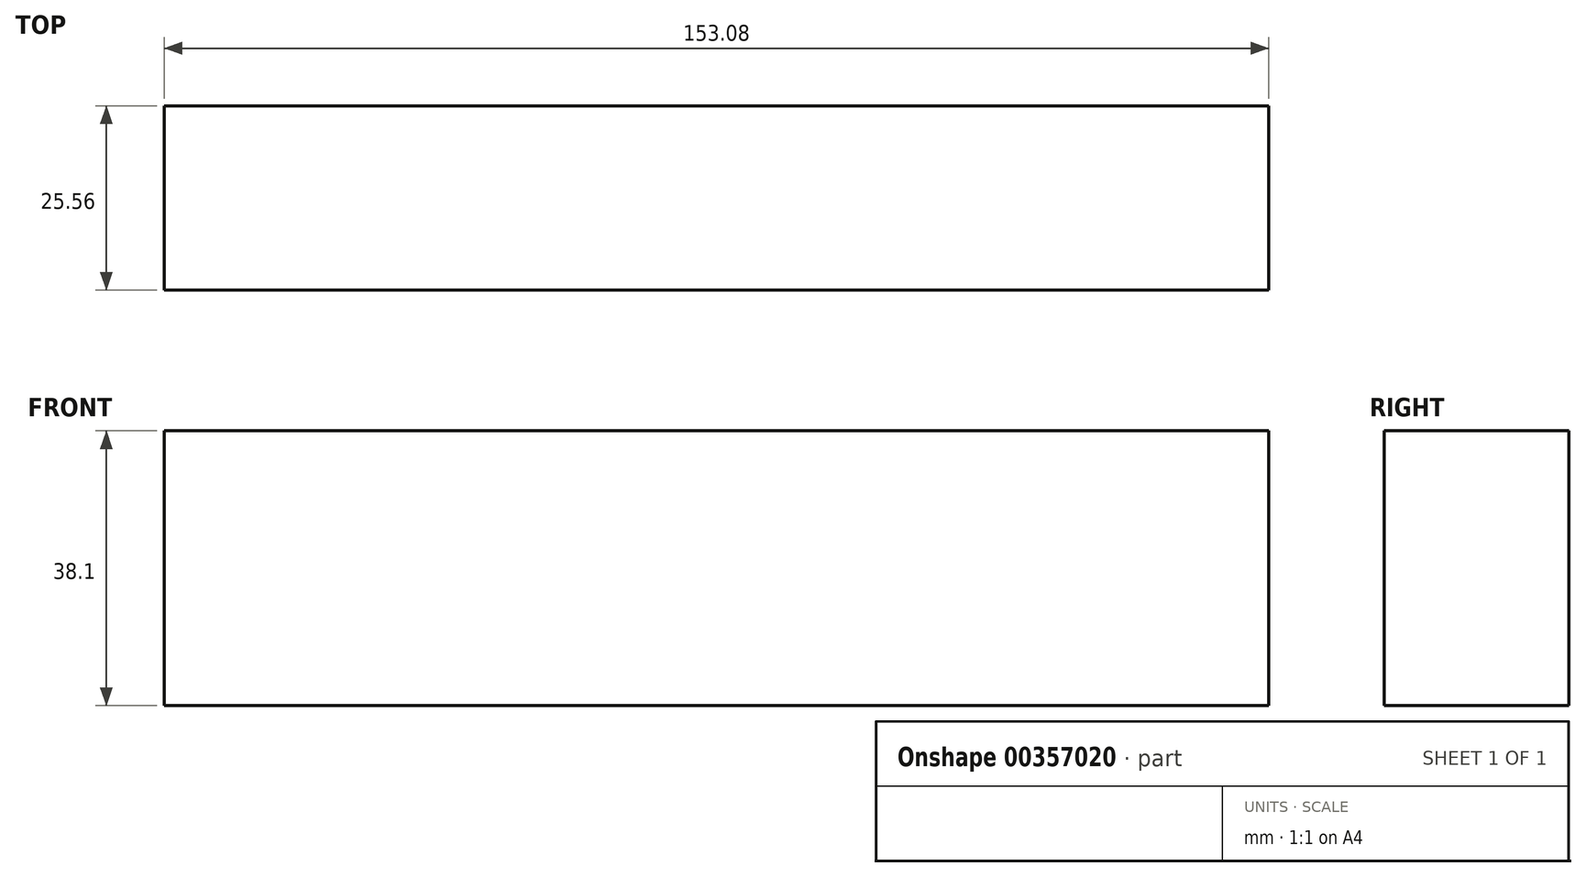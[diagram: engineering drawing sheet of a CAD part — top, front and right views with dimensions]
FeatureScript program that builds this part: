
annotation { "Feature Type Name" : "Feature", "Feature Type Description" : "" }
export const myFeature = defineFeature(function(context is Context, id is Id, definition is map)
    precondition{}
    {
        {
            var Q0;
            Q0=qCreatedBy(makeId("Top.planeOp"),FACE);
            var sketch = newSketch(context, id + "F0", { "sketchPlane" : qUnion([Q0])});
            skLineSegment(sketch, "E0.bottom", {"start": v(-76.54, 12.78) * mm, "end": v(76.54, 12.78) * mm});
            skLineSegment(sketch, "E0.top", {"start": v(-76.54, -12.78) * mm, "end": v(76.54, -12.78) * mm});
            skLineSegment(sketch, "E0.left", {"start": v(-76.54, 12.78) * mm, "end": v(-76.54, -12.78) * mm});
            skLineSegment(sketch, "E0.right", {"start": v(76.54, 12.78) * mm, "end": v(76.54, -12.78) * mm});
            skPoint(sketch, "E0.middle", {"position": v(0, 0) * mm});
            skSolve(sketch);
        }
        {
            var Q0;
            Q0=makeQuery(id+"F0.imprint","IMPRINT",FACE,{"disambiguationData":[TD([[makeQuery(id+"F0.imprint","IMPRINT",EDGE,{"derivedFrom":sQuery(id+"F0.wireOp",EDGE,"E0.bottom")}),-1.0]])]});
            extrude(context, id + "F1", {"entities" : qUnion([Q0]), "depth" : 38.1 * mm});
        }
    });
